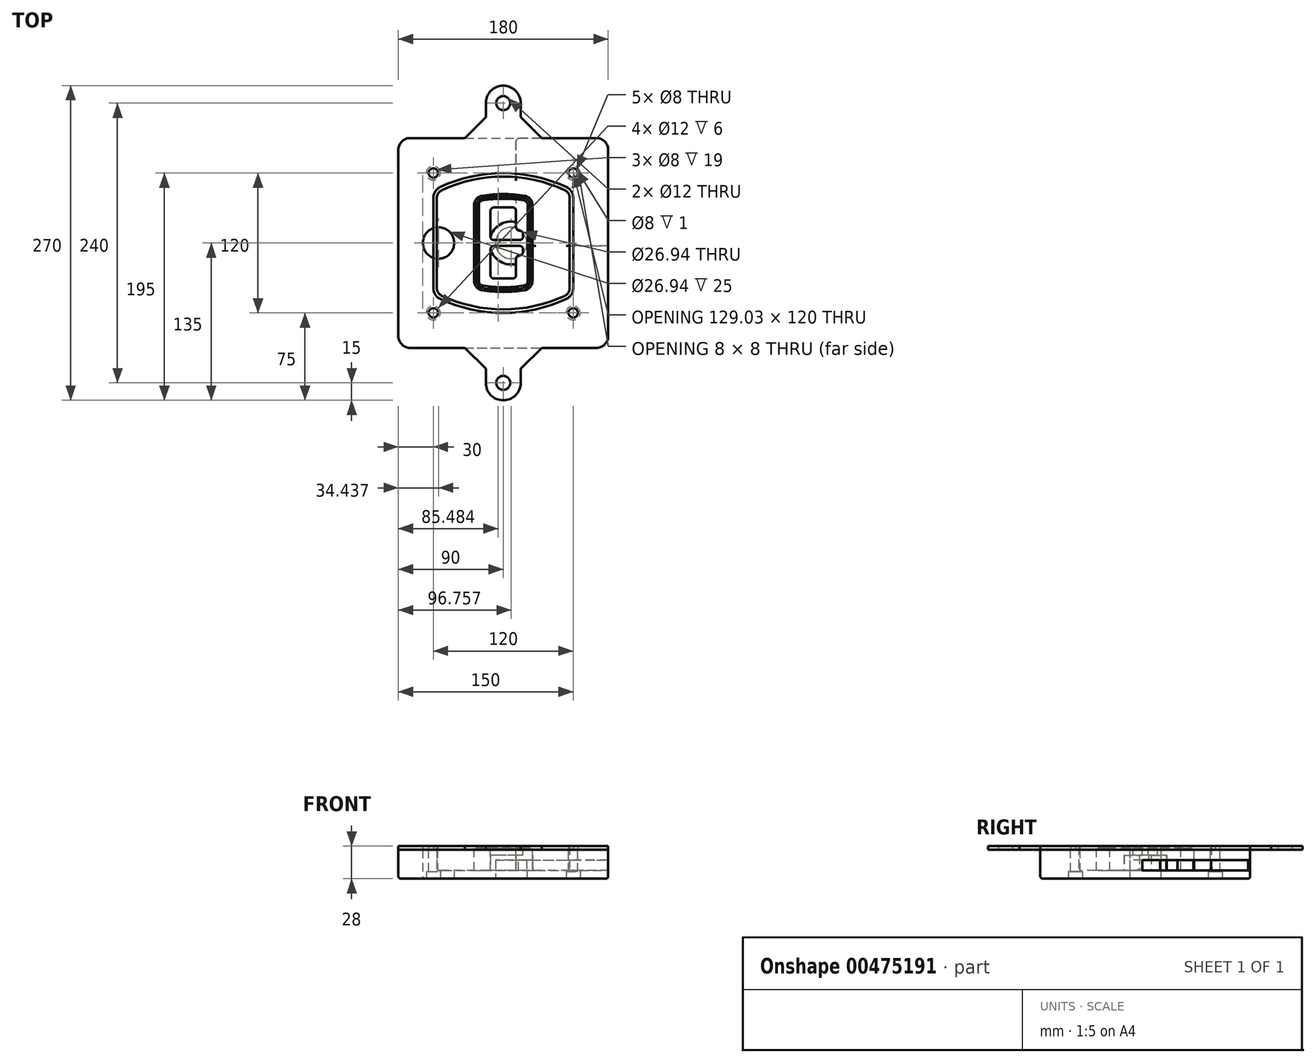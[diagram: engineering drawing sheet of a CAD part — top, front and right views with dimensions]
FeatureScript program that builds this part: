
annotation { "Feature Type Name" : "Feature", "Feature Type Description" : "" }
export const myFeature = defineFeature(function(context is Context, id is Id, definition is map)
    precondition{}
    {
        {
            var Q0;
            Q0=qCreatedBy(makeId("Top.planeOp"),FACE);
            var sketch = newSketch(context, id + "F0", { "sketchPlane" : qUnion([Q0])});
            skPoint(sketch, "E0.rect.middle", {"position": v(0, 0) * mm});
            skLineSegment(sketch, "E1.bottom", {"start": v(-80, -90) * mm, "end": v(80, -90) * mm});
            skLineSegment(sketch, "E1.top", {"start": v(-80, 90) * mm, "end": v(80, 90) * mm});
            skLineSegment(sketch, "E1.left", {"start": v(-90, -80) * mm, "end": v(-90, 80) * mm});
            skLineSegment(sketch, "E1.right", {"start": v(90, -80) * mm, "end": v(90, 80) * mm});
            skLineSegment(sketch, "E2", {"start": v(-90, 90) * mm, "end": v(90, -90) * mm, "construction": true});
            skLineSegment(sketch, "E3", {"start": v(90, 90) * mm, "end": v(-90, -90) * mm, "construction": true});
            skCircle(sketch, "E4", {"center": v(-60, 60) * mm, "radius": 4 * mm});
            skCircle(sketch, "E5", {"center": v(60, 60) * mm, "radius": 4 * mm});
            skCircle(sketch, "E6", {"center": v(60, -60) * mm, "radius": 4 * mm});
            skCircle(sketch, "E7", {"center": v(-60, -60) * mm, "radius": 4 * mm});
            skLineSegment(sketch, "E8", {"start": v(-60, 60) * mm, "end": v(60, 60) * mm, "construction": true});
            skLineSegment(sketch, "E9", {"start": v(60, 60) * mm, "end": v(60, -60) * mm, "construction": true});
            skLineSegment(sketch, "E10", {"start": v(60, -60) * mm, "end": v(-60, -60) * mm, "construction": true});
            skLineSegment(sketch, "E11", {"start": v(-60, -60) * mm, "end": v(-60, 60) * mm, "construction": true});
            skLineSegment(sketch, "E12", {"start": v(-60, 38.83) * mm, "end": v(-60, -38.83) * mm});
            skLineSegment(sketch, "E13", {"start": v(60, 38.83) * mm, "end": v(60, -38.83) * mm});
            skArc(sketch, "E14", {"start": v(54.26, 47.88) * mm, "mid": v(0, 60) * mm, "end": v(-54.26, 47.88) * mm});
            skArc(sketch, "E15", {"start": v(-54.26, -47.88) * mm, "mid": v(0, -60) * mm, "end": v(54.26, -47.88) * mm});
            skLineSegment(sketch, "E16", {"start": v(-60, 0) * mm, "end": v(60, 0) * mm, "construction": true});
            skPoint(sketch, "E17.visualSharp", {"position": v(-60, -45) * mm});
            skArc(sketch, "E17.filletArc", {"start": v(-60, -38.83) * mm, "mid": v(-58.44, -44.2) * mm, "end": v(-54.26, -47.88) * mm});
            skPoint(sketch, "E18.visualSharp", {"position": v(-60, 45) * mm});
            skArc(sketch, "E18.filletArc", {"start": v(-54.26, 47.88) * mm, "mid": v(-58.44, 44.2) * mm, "end": v(-60, 38.83) * mm});
            skPoint(sketch, "E19.visualSharp", {"position": v(60, 45) * mm});
            skArc(sketch, "E19.filletArc", {"start": v(60, 38.83) * mm, "mid": v(58.44, 44.2) * mm, "end": v(54.26, 47.88) * mm});
            skPoint(sketch, "E20.visualSharp", {"position": v(60, -45) * mm});
            skArc(sketch, "E20.filletArc", {"start": v(54.26, -47.88) * mm, "mid": v(58.44, -44.2) * mm, "end": v(60, -38.83) * mm});
            skPoint(sketch, "E21.visualSharp", {"position": v(-90, 90) * mm});
            skArc(sketch, "E21.filletArc", {"start": v(-80, 90) * mm, "mid": v(-87.07, 87.07) * mm, "end": v(-90, 80) * mm});
            skPoint(sketch, "E22.visualSharp", {"position": v(90, 90) * mm});
            skArc(sketch, "E22.filletArc", {"start": v(90, 80) * mm, "mid": v(87.07, 87.07) * mm, "end": v(80, 90) * mm});
            skPoint(sketch, "E23.visualSharp", {"position": v(90, -90) * mm});
            skArc(sketch, "E23.filletArc", {"start": v(80, -90) * mm, "mid": v(87.07, -87.07) * mm, "end": v(90, -80) * mm});
            skPoint(sketch, "E24.visualSharp", {"position": v(-90, -90) * mm});
            skArc(sketch, "E24.filletArc", {"start": v(-90, -80) * mm, "mid": v(-87.07, -87.07) * mm, "end": v(-80, -90) * mm});
            skArc(sketch, "E25.0", {"start": v(57, 38.83) * mm, "mid": v(55.9, 42.58) * mm, "end": v(52.98, 45.17) * mm});
            skLineSegment(sketch, "E25.1", {"start": v(57, 38.83) * mm, "end": v(57, -38.83) * mm});
            skArc(sketch, "E25.2", {"start": v(52.98, -45.17) * mm, "mid": v(55.9, -42.58) * mm, "end": v(57, -38.83) * mm});
            skArc(sketch, "E25.3", {"start": v(-52.98, -45.17) * mm, "mid": v(0, -57) * mm, "end": v(52.98, -45.17) * mm});
            skArc(sketch, "E25.4", {"start": v(-57, -38.83) * mm, "mid": v(-55.9, -42.58) * mm, "end": v(-52.98, -45.17) * mm});
            skArc(sketch, "E25.5", {"start": v(52.98, 45.17) * mm, "mid": v(0, 57) * mm, "end": v(-52.98, 45.17) * mm});
            skLineSegment(sketch, "E25.6", {"start": v(-57, 38.83) * mm, "end": v(-57, -38.83) * mm});
            skArc(sketch, "E25.7", {"start": v(-52.98, 45.17) * mm, "mid": v(-55.9, 42.58) * mm, "end": v(-57, 38.83) * mm});
            skArc(sketch, "E26.0", {"start": v(-55.96, 51.5) * mm, "mid": v(-61.82, 46.33) * mm, "end": v(-64, 38.83) * mm});
            skArc(sketch, "E26.1", {"start": v(55.96, 51.5) * mm, "mid": v(0, 64) * mm, "end": v(-55.96, 51.5) * mm});
            skArc(sketch, "E26.2", {"start": v(64, 38.83) * mm, "mid": v(61.82, 46.33) * mm, "end": v(55.96, 51.5) * mm});
            skLineSegment(sketch, "E26.3", {"start": v(64, 38.83) * mm, "end": v(64, -38.83) * mm});
            skArc(sketch, "E26.4", {"start": v(55.96, -51.5) * mm, "mid": v(61.82, -46.33) * mm, "end": v(64, -38.83) * mm});
            skLineSegment(sketch, "E26.5", {"start": v(-64, 38.83) * mm, "end": v(-64, -38.83) * mm});
            skArc(sketch, "E26.6", {"start": v(-55.96, -51.5) * mm, "mid": v(0, -64) * mm, "end": v(55.96, -51.5) * mm});
            skArc(sketch, "E26.7", {"start": v(-64, -38.83) * mm, "mid": v(-61.82, -46.33) * mm, "end": v(-55.96, -51.5) * mm});
            skSolve(sketch);
        }
        {
            var Q0;
            Q0=makeQuery(id+"F0.imprint","IMPRINT",FACE,{"disambiguationData":[TD([[makeQuery(id+"F0.imprint","IMPRINT",EDGE,{"derivedFrom":sQuery(id+"F0.wireOp",EDGE,"E1.bottom")}),1.0]])]});
            var Q1;
            Q1=makeQuery(id+"F0.imprint","IMPRINT",FACE,{"disambiguationData":[TD([[makeQuery(id+"F0.imprint","IMPRINT",EDGE,{"derivedFrom":sQuery(id+"F0.wireOp",EDGE,"E12")}),1.0]])]});
            var Q2;
            Q2=makeQuery(id+"F0.imprint","IMPRINT",FACE,{"disambiguationData":[TD([[makeQuery(id+"F0.imprint","IMPRINT",EDGE,{"derivedFrom":sQuery(id+"F0.wireOp",EDGE,"E25.0")}),1.0]])]});
            var Q3;
            Q3=makeQuery(id+"F0.imprint","IMPRINT",FACE,{"disambiguationData":[TD([[makeQuery(id+"F0.imprint","IMPRINT",EDGE,{"derivedFrom":sQuery(id+"F0.wireOp",EDGE,"E12")}),-1.0]])]});
            extrude(context, id + "F1", {"entities" : qUnion([Q0, Q1, Q2, Q3]), "oppositeDirection" : true, "depth" : 25 * mm});
        }
        {
            var Q0;
            Q0=makeQuery(id+"F0.imprint","IMPRINT",FACE,{"disambiguationData":[TD([[makeQuery(id+"F0.imprint","IMPRINT",EDGE,{"derivedFrom":sQuery(id+"F0.wireOp",EDGE,"E12")}),1.0]])]});
            extrude(context, id + "F2", {"entities" : qUnion([Q0]), "operationType" : NewBodyOperationType.ADD, "depth" : 3 * mm});
        }
        {
            var Q0;
            Q0=makeQuery(id+"F0.imprint","IMPRINT",FACE,{"disambiguationData":[TD([[makeQuery(id+"F0.imprint","IMPRINT",EDGE,{"derivedFrom":sQuery(id+"F0.wireOp",EDGE,"E25.0")}),1.0]])]});
            extrude(context, id + "F3", {"entities" : qUnion([Q0]), "operationType" : NewBodyOperationType.REMOVE, "oppositeDirection" : true, "depth" : 18 * mm});
        }
        {
            var Q0;
            Q0=makeQuery(id+"F2.opExtrude","CAP_FACE",FACE,{"disambiguationData":[OSD([sQuery(id+"F0.wireOp",EDGE,"E12"),sQuery(id+"F0.wireOp",EDGE,"E13"),sQuery(id+"F0.wireOp",EDGE,"E14"),sQuery(id+"F0.wireOp",EDGE,"E15"),sQuery(id+"F0.wireOp",EDGE,"E17.filletArc"),sQuery(id+"F0.wireOp",EDGE,"E18.filletArc"),sQuery(id+"F0.wireOp",EDGE,"E19.filletArc"),sQuery(id+"F0.wireOp",EDGE,"E20.filletArc"),sQuery(id+"F0.wireOp",EDGE,"E25.0"),sQuery(id+"F0.wireOp",EDGE,"E25.1"),sQuery(id+"F0.wireOp",EDGE,"E25.2"),sQuery(id+"F0.wireOp",EDGE,"E25.3"),sQuery(id+"F0.wireOp",EDGE,"E25.4"),sQuery(id+"F0.wireOp",EDGE,"E25.5"),sQuery(id+"F0.wireOp",EDGE,"E25.6"),sQuery(id+"F0.wireOp",EDGE,"E25.7")])],"isStart":false});
            var sketch = newSketch(context, id + "F4", { "sketchPlane" : qUnion([Q0])});
            skArc(sketch, "E27.0", {"start": v(-18.34, -40.45) * mm, "mid": v(0, -42) * mm, "end": v(18.34, -40.45) * mm});
            skArc(sketch, "E28.0", {"start": v(18.34, 40.45) * mm, "mid": v(0, 42) * mm, "end": v(-18.34, 40.45) * mm});
            skLineSegment(sketch, "E29", {"start": v(-25, 32.57) * mm, "end": v(-25, -32.57) * mm});
            skLineSegment(sketch, "E30", {"start": v(25, 32.57) * mm, "end": v(25, -32.57) * mm});
            skLineSegment(sketch, "E31", {"start": v(-25, 39.1) * mm, "end": v(25, 39.1) * mm, "construction": true});
            skLineSegment(sketch, "E32", {"start": v(-25, -39.1) * mm, "end": v(25, -39.1) * mm, "construction": true});
            skPoint(sketch, "E33.visualSharp", {"position": v(-25, 39.1) * mm});
            skArc(sketch, "E33.filletArc", {"start": v(-18.34, 40.45) * mm, "mid": v(-23.11, 37.73) * mm, "end": v(-25, 32.57) * mm});
            skPoint(sketch, "E34.visualSharp", {"position": v(25, 39.1) * mm});
            skArc(sketch, "E34.filletArc", {"start": v(25, 32.57) * mm, "mid": v(23.11, 37.73) * mm, "end": v(18.34, 40.45) * mm});
            skPoint(sketch, "E35.visualSharp", {"position": v(25, -39.1) * mm});
            skArc(sketch, "E35.filletArc", {"start": v(18.34, -40.45) * mm, "mid": v(23.11, -37.73) * mm, "end": v(25, -32.57) * mm});
            skPoint(sketch, "E36.visualSharp", {"position": v(-25, -39.1) * mm});
            skArc(sketch, "E36.filletArc", {"start": v(-25, -32.57) * mm, "mid": v(-23.11, -37.73) * mm, "end": v(-18.34, -40.45) * mm});
            skArc(sketch, "E37.0", {"start": v(52.98, 45.17) * mm, "mid": v(0, 57) * mm, "end": v(-52.98, 45.17) * mm});
            skArc(sketch, "E37.1", {"start": v(-52.98, 45.17) * mm, "mid": v(-55.9, 42.58) * mm, "end": v(-57, 38.83) * mm});
            skLineSegment(sketch, "E37.2", {"start": v(-57, 38.83) * mm, "end": v(-57, -38.83) * mm});
            skArc(sketch, "E37.3", {"start": v(-57, -38.83) * mm, "mid": v(-55.9, -42.58) * mm, "end": v(-52.98, -45.17) * mm});
            skArc(sketch, "E37.4", {"start": v(-52.98, -45.17) * mm, "mid": v(0, -57) * mm, "end": v(52.98, -45.17) * mm});
            skArc(sketch, "E37.5", {"start": v(52.98, -45.17) * mm, "mid": v(55.9, -42.58) * mm, "end": v(57, -38.83) * mm});
            skLineSegment(sketch, "E37.6", {"start": v(57, 38.83) * mm, "end": v(57, -38.83) * mm});
            skArc(sketch, "E37.7", {"start": v(57, 38.83) * mm, "mid": v(55.9, 42.58) * mm, "end": v(52.98, 45.17) * mm});
            skLineSegment(sketch, "E38.0", {"start": v(23, 32.57) * mm, "end": v(23, -32.57) * mm});
            skArc(sketch, "E38.1", {"start": v(18, -38.48) * mm, "mid": v(21.58, -36.44) * mm, "end": v(23, -32.57) * mm});
            skArc(sketch, "E38.2", {"start": v(-18, -38.48) * mm, "mid": v(0, -40) * mm, "end": v(18, -38.48) * mm});
            skArc(sketch, "E38.3", {"start": v(-23, -32.57) * mm, "mid": v(-21.58, -36.44) * mm, "end": v(-18, -38.48) * mm});
            skLineSegment(sketch, "E38.4", {"start": v(-23, 32.57) * mm, "end": v(-23, -32.57) * mm});
            skArc(sketch, "E38.5", {"start": v(23, 32.57) * mm, "mid": v(21.58, 36.44) * mm, "end": v(18, 38.48) * mm});
            skArc(sketch, "E38.6", {"start": v(-18, 38.48) * mm, "mid": v(-21.58, 36.44) * mm, "end": v(-23, 32.57) * mm});
            skArc(sketch, "E38.7", {"start": v(18, 38.48) * mm, "mid": v(0, 40) * mm, "end": v(-18, 38.48) * mm});
            skArc(sketch, "E39.0", {"start": v(21, 32.57) * mm, "mid": v(20.06, 35.15) * mm, "end": v(17.67, 36.5) * mm});
            skLineSegment(sketch, "E39.1", {"start": v(21, 32.57) * mm, "end": v(21, -32.57) * mm});
            skArc(sketch, "E39.2", {"start": v(17.67, -36.5) * mm, "mid": v(20.06, -35.15) * mm, "end": v(21, -32.57) * mm});
            skArc(sketch, "E39.3", {"start": v(-17.67, -36.5) * mm, "mid": v(0, -38) * mm, "end": v(17.67, -36.5) * mm});
            skArc(sketch, "E39.4", {"start": v(-21, -32.57) * mm, "mid": v(-20.06, -35.15) * mm, "end": v(-17.67, -36.5) * mm});
            skArc(sketch, "E39.5", {"start": v(17.67, 36.5) * mm, "mid": v(0, 38) * mm, "end": v(-17.67, 36.5) * mm});
            skLineSegment(sketch, "E39.6", {"start": v(-21, 32.57) * mm, "end": v(-21, -32.57) * mm});
            skArc(sketch, "E39.7", {"start": v(-17.67, 36.5) * mm, "mid": v(-20.06, 35.15) * mm, "end": v(-21, 32.57) * mm});
            skLineSegment(sketch, "E40", {"start": v(-25, 0) * mm, "end": v(25, 0) * mm, "construction": true});
            skLineSegment(sketch, "E41", {"start": v(-11, 5.5) * mm, "end": v(-11, 27.5) * mm});
            skLineSegment(sketch, "E42", {"start": v(-8, 30.5) * mm, "end": v(8, 30.5) * mm});
            skLineSegment(sketch, "E43", {"start": v(11, 27.5) * mm, "end": v(11, 13.5) * mm});
            skLineSegment(sketch, "E44", {"start": v(14, 10.5) * mm, "end": v(14, 10.5) * mm});
            skLineSegment(sketch, "E45", {"start": v(17, 7.5) * mm, "end": v(17, 5.5) * mm});
            skLineSegment(sketch, "E46", {"start": v(14, 2.5) * mm, "end": v(-8, 2.5) * mm});
            skPoint(sketch, "E47.visualSharp", {"position": v(-11, 30.5) * mm});
            skArc(sketch, "E47.filletArc", {"start": v(-8, 30.5) * mm, "mid": v(-10.12, 29.62) * mm, "end": v(-11, 27.5) * mm});
            skPoint(sketch, "E48.visualSharp", {"position": v(11, 30.5) * mm});
            skArc(sketch, "E48.filletArc", {"start": v(11, 27.5) * mm, "mid": v(10.12, 29.62) * mm, "end": v(8, 30.5) * mm});
            skPoint(sketch, "E49.visualSharp", {"position": v(11, 10.5) * mm});
            skArc(sketch, "E49.filletArc", {"start": v(11, 13.5) * mm, "mid": v(11.88, 11.38) * mm, "end": v(14, 10.5) * mm});
            skPoint(sketch, "E50.visualSharp", {"position": v(17, 10.5) * mm});
            skArc(sketch, "E50.filletArc", {"start": v(17, 7.5) * mm, "mid": v(16.12, 9.62) * mm, "end": v(14, 10.5) * mm});
            skPoint(sketch, "E51.visualSharp", {"position": v(17, 2.5) * mm});
            skArc(sketch, "E51.filletArc", {"start": v(14, 2.5) * mm, "mid": v(16.12, 3.38) * mm, "end": v(17, 5.5) * mm});
            skPoint(sketch, "E52.visualSharp", {"position": v(-11, 2.5) * mm});
            skArc(sketch, "E52.filletArc", {"start": v(-11, 5.5) * mm, "mid": v(-10.12, 3.38) * mm, "end": v(-8, 2.5) * mm});
            skLineSegment(sketch, "E53.0.MirrorCS", {"start": v(14, -2.5) * mm, "end": v(-8, -2.5) * mm});
            skArc(sketch, "E54.0.MirrorCS", {"start": v(-11, -5.5) * mm, "mid": v(-10.12, -3.38) * mm, "end": v(-8, -2.5) * mm});
            skLineSegment(sketch, "E55.0.MirrorCS", {"start": v(-11, -5.5) * mm, "end": v(-11, -27.5) * mm});
            skArc(sketch, "E56.0.MirrorCS", {"start": v(-8, -30.5) * mm, "mid": v(-10.12, -29.62) * mm, "end": v(-11, -27.5) * mm});
            skLineSegment(sketch, "E57.0.MirrorCS", {"start": v(-8, -30.5) * mm, "end": v(8, -30.5) * mm});
            skArc(sketch, "E58.0.MirrorCS", {"start": v(11, -27.5) * mm, "mid": v(10.12, -29.62) * mm, "end": v(8, -30.5) * mm});
            skLineSegment(sketch, "E59.0.MirrorCS", {"start": v(11, -27.5) * mm, "end": v(11, -13.5) * mm});
            skArc(sketch, "E60.0.MirrorCS", {"start": v(11, -13.5) * mm, "mid": v(11.88, -11.38) * mm, "end": v(14, -10.5) * mm});
            skArc(sketch, "E61.0.MirrorCS", {"start": v(17, -7.5) * mm, "mid": v(16.12, -9.62) * mm, "end": v(14, -10.5) * mm});
            skLineSegment(sketch, "E62.0.MirrorCS", {"start": v(17, -7.5) * mm, "end": v(17, -5.5) * mm});
            skArc(sketch, "E63.0.MirrorCS", {"start": v(14, -2.5) * mm, "mid": v(16.12, -3.38) * mm, "end": v(17, -5.5) * mm});
            skSolve(sketch);
        }
        {
            var Q0;
            Q0=makeQuery(id+"F4.imprint","IMPRINT",FACE,{"disambiguationData":[TD([[makeQuery(id+"F4.imprint","IMPRINT",EDGE,{"derivedFrom":sQuery(id+"F4.wireOp",EDGE,"E27.0")}),1.0]])]});
            var Q1;
            Q1=makeQuery(id+"F4.imprint","IMPRINT",FACE,{"disambiguationData":[TD([[makeQuery(id+"F4.imprint","IMPRINT",EDGE,{"derivedFrom":sQuery(id+"F4.wireOp",EDGE,"E38.0")}),-1.0]])]});
            var Q2;
            Q2=makeQuery(id+"F4.imprint","IMPRINT",FACE,{"disambiguationData":[TD([[makeQuery(id+"F4.imprint","IMPRINT",EDGE,{"derivedFrom":sQuery(id+"F4.wireOp",EDGE,"E39.0")}),1.0]])]});
            extrude(context, id + "F5", {"entities" : qUnion([Q0, Q1, Q2]), "operationType" : NewBodyOperationType.ADD, "endBound" : BoundingType.UP_TO_NEXT, "oppositeDirection" : true, "depth" : 25 * mm});
        }
        {
            var Q0;
            Q0=makeQuery(id+"F4.imprint","IMPRINT",FACE,{"disambiguationData":[TD([[makeQuery(id+"F4.imprint","IMPRINT",EDGE,{"derivedFrom":sQuery(id+"F4.wireOp",EDGE,"E38.0")}),-1.0]])]});
            extrude(context, id + "F6", {"entities" : qUnion([Q0]), "operationType" : NewBodyOperationType.REMOVE, "oppositeDirection" : true, "depth" : 2 * mm});
        }
        {
            var Q0;
            Q0=makeQuery(id+"F1.opExtrude","CAP_FACE",FACE,{"disambiguationData":[OSD([sQuery(id+"F0.wireOp",EDGE,"E1.bottom"),sQuery(id+"F0.wireOp",EDGE,"E1.top"),sQuery(id+"F0.wireOp",EDGE,"E1.left"),sQuery(id+"F0.wireOp",EDGE,"E1.right"),sQuery(id+"F0.wireOp",EDGE,"E4"),sQuery(id+"F0.wireOp",EDGE,"E5"),sQuery(id+"F0.wireOp",EDGE,"E6"),sQuery(id+"F0.wireOp",EDGE,"E7"),sQuery(id+"F0.wireOp",EDGE,"E21.filletArc"),sQuery(id+"F0.wireOp",EDGE,"E22.filletArc"),sQuery(id+"F0.wireOp",EDGE,"E23.filletArc"),sQuery(id+"F0.wireOp",EDGE,"E24.filletArc")])],"isStart":false});
            var sketch = newSketch(context, id + "F7", { "sketchPlane" : qUnion([Q0])});
            skCircle(sketch, "E64", {"center": v(6.76, 0) * mm, "radius": 13.47 * mm});
            skCircle(sketch, "E65", {"center": v(-55.56, 0) * mm, "radius": 13.47 * mm});
            skLineSegment(sketch, "E66", {"start": v(90, 0) * mm, "end": v(-90, 0) * mm});
            skCircle(sketch, "E67", {"center": v(6.76, 0) * mm, "radius": 18.47 * mm});
            skCircle(sketch, "E68", {"center": v(60, -60) * mm, "radius": 6 * mm});
            skCircle(sketch, "E69", {"center": v(-60, -60) * mm, "radius": 6 * mm});
            skCircle(sketch, "E70", {"center": v(-60, 60) * mm, "radius": 6 * mm});
            skCircle(sketch, "E71", {"center": v(60, 60) * mm, "radius": 6 * mm});
            skSolve(sketch);
        }
        {
            var Q0;
            {var subQ1=sQuery(id+"F7.wireOp",EDGE,"E66");var subQ4=sQuery(id+"F7.wireOp",EDGE,"E64");var subQ6=makeQuery(id+"F7.imprint","INTERSECT",VERTEX,{"disambiguationData":[OD(0.0)],"derivedFrom":[subQ4,subQ1]});Q0=makeQuery(id+"F7.imprint","IMPRINT",FACE,{"disambiguationData":[TD([[makeQuery(id+"F7.imprint","IMPRINT",EDGE,{"disambiguationData":[TD([[subQ6,-1.0]])],"derivedFrom":subQ4}),-1.0]])]});}
            var Q1;
            {var subQ0=sQuery(id+"F7.wireOp",EDGE,"E66");var subQ1=sQuery(id+"F7.wireOp",EDGE,"E64");var subQ3=makeQuery(id+"F7.imprint","INTERSECT",VERTEX,{"disambiguationData":[OD(0.0)],"derivedFrom":[subQ1,subQ0]});Q1=makeQuery(id+"F7.imprint","IMPRINT",FACE,{"disambiguationData":[TD([[makeQuery(id+"F7.imprint","IMPRINT",EDGE,{"disambiguationData":[TD([[subQ3,-1.0]])],"derivedFrom":subQ1}),1.0]])]});}
            var Q2;
            {var subQ0=sQuery(id+"F7.wireOp",EDGE,"E66");var subQ1=sQuery(id+"F7.wireOp",EDGE,"E64");var subQ3=makeQuery(id+"F7.imprint","INTERSECT",VERTEX,{"disambiguationData":[OD(0.0)],"derivedFrom":[subQ1,subQ0]});Q2=makeQuery(id+"F7.imprint","IMPRINT",FACE,{"disambiguationData":[TD([[makeQuery(id+"F7.imprint","IMPRINT",EDGE,{"disambiguationData":[TD([[subQ3,1.0]])],"derivedFrom":subQ1}),1.0]])]});}
            var Q3;
            {var subQ1=sQuery(id+"F7.wireOp",EDGE,"E66");var subQ4=sQuery(id+"F7.wireOp",EDGE,"E64");var subQ6=makeQuery(id+"F7.imprint","INTERSECT",VERTEX,{"disambiguationData":[OD(0.0)],"derivedFrom":[subQ4,subQ1]});Q3=makeQuery(id+"F7.imprint","IMPRINT",FACE,{"disambiguationData":[TD([[makeQuery(id+"F7.imprint","IMPRINT",EDGE,{"disambiguationData":[TD([[subQ6,1.0]])],"derivedFrom":subQ4}),-1.0]])]});}
            extrude(context, id + "F8", {"entities" : qUnion([Q0, Q1, Q2, Q3]), "operationType" : NewBodyOperationType.ADD, "oppositeDirection" : true, "depth" : 20 * mm});
        }
        {
            var Q0;
            {var subQ0=sQuery(id+"F7.wireOp",EDGE,"E66");var subQ1=sQuery(id+"F7.wireOp",EDGE,"E64");var subQ3=makeQuery(id+"F7.imprint","INTERSECT",VERTEX,{"disambiguationData":[OD(0.0)],"derivedFrom":[subQ1,subQ0]});Q0=makeQuery(id+"F7.imprint","IMPRINT",FACE,{"disambiguationData":[TD([[makeQuery(id+"F7.imprint","IMPRINT",EDGE,{"disambiguationData":[TD([[subQ3,-1.0]])],"derivedFrom":subQ1}),1.0]])]});}
            var Q1;
            {var subQ0=sQuery(id+"F7.wireOp",EDGE,"E66");var subQ1=sQuery(id+"F7.wireOp",EDGE,"E64");var subQ3=makeQuery(id+"F7.imprint","INTERSECT",VERTEX,{"disambiguationData":[OD(0.0)],"derivedFrom":[subQ1,subQ0]});Q1=makeQuery(id+"F7.imprint","IMPRINT",FACE,{"disambiguationData":[TD([[makeQuery(id+"F7.imprint","IMPRINT",EDGE,{"disambiguationData":[TD([[subQ3,1.0]])],"derivedFrom":subQ1}),1.0]])]});}
            extrude(context, id + "F9", {"entities" : qUnion([Q0, Q1]), "operationType" : NewBodyOperationType.REMOVE, "oppositeDirection" : true, "depth" : 16 * mm});
        }
        {
            var Q0;
            {var subQ0=sQuery(id+"F7.wireOp",EDGE,"E66");var subQ1=sQuery(id+"F7.wireOp",EDGE,"E65");var subQ3=makeQuery(id+"F7.imprint","INTERSECT",VERTEX,{"disambiguationData":[OD(0.0)],"derivedFrom":[subQ1,subQ0]});Q0=makeQuery(id+"F7.imprint","IMPRINT",FACE,{"disambiguationData":[TD([[makeQuery(id+"F7.imprint","IMPRINT",EDGE,{"disambiguationData":[TD([[subQ3,-1.0]])],"derivedFrom":subQ1}),1.0]])]});}
            var Q1;
            {var subQ0=sQuery(id+"F7.wireOp",EDGE,"E66");var subQ1=sQuery(id+"F7.wireOp",EDGE,"E65");var subQ3=makeQuery(id+"F7.imprint","INTERSECT",VERTEX,{"disambiguationData":[OD(0.0)],"derivedFrom":[subQ1,subQ0]});Q1=makeQuery(id+"F7.imprint","IMPRINT",FACE,{"disambiguationData":[TD([[makeQuery(id+"F7.imprint","IMPRINT",EDGE,{"disambiguationData":[TD([[subQ3,1.0]])],"derivedFrom":subQ1}),1.0]])]});}
            extrude(context, id + "F10", {"entities" : qUnion([Q0, Q1]), "operationType" : NewBodyOperationType.REMOVE, "oppositeDirection" : true, "depth" : 25 * mm});
        }
        {
            var Q0;
            Q0=makeQuery(id+"F7.imprint","IMPRINT",FACE,{"disambiguationData":[TD([[makeQuery(id+"F7.imprint","IMPRINT",EDGE,{"derivedFrom":sQuery(id+"F7.wireOp",EDGE,"E68")}),1.0]])]});
            var Q1;
            Q1=makeQuery(id+"F7.imprint","IMPRINT",FACE,{"disambiguationData":[TD([[makeQuery(id+"F7.imprint","IMPRINT",EDGE,{"derivedFrom":makeQuery(id+"F1.opExtrude","CAP_EDGE",EDGE,{"disambiguationData":[OSD([sQuery(id+"F0.wireOp",EDGE,"E5")])],"isStart":false})}),-1.0]])]});
            var Q2;
            Q2=makeQuery(id+"F7.imprint","IMPRINT",FACE,{"disambiguationData":[TD([[makeQuery(id+"F7.imprint","IMPRINT",EDGE,{"derivedFrom":sQuery(id+"F7.wireOp",EDGE,"E69")}),1.0]])]});
            var Q3;
            Q3=makeQuery(id+"F7.imprint","IMPRINT",FACE,{"disambiguationData":[TD([[makeQuery(id+"F7.imprint","IMPRINT",EDGE,{"derivedFrom":makeQuery(id+"F1.opExtrude","CAP_EDGE",EDGE,{"disambiguationData":[OSD([sQuery(id+"F0.wireOp",EDGE,"E4")])],"isStart":false})}),-1.0]])]});
            var Q4;
            Q4=makeQuery(id+"F7.imprint","IMPRINT",FACE,{"disambiguationData":[TD([[makeQuery(id+"F7.imprint","IMPRINT",EDGE,{"derivedFrom":sQuery(id+"F7.wireOp",EDGE,"E70")}),1.0]])]});
            var Q5;
            Q5=makeQuery(id+"F7.imprint","IMPRINT",FACE,{"disambiguationData":[TD([[makeQuery(id+"F7.imprint","IMPRINT",EDGE,{"derivedFrom":makeQuery(id+"F1.opExtrude","CAP_EDGE",EDGE,{"disambiguationData":[OSD([sQuery(id+"F0.wireOp",EDGE,"E7")])],"isStart":false})}),-1.0]])]});
            var Q6;
            Q6=makeQuery(id+"F7.imprint","IMPRINT",FACE,{"disambiguationData":[TD([[makeQuery(id+"F7.imprint","IMPRINT",EDGE,{"derivedFrom":sQuery(id+"F7.wireOp",EDGE,"E71")}),1.0]])]});
            var Q7;
            Q7=makeQuery(id+"F7.imprint","IMPRINT",FACE,{"disambiguationData":[TD([[makeQuery(id+"F7.imprint","IMPRINT",EDGE,{"derivedFrom":makeQuery(id+"F1.opExtrude","CAP_EDGE",EDGE,{"disambiguationData":[OSD([sQuery(id+"F0.wireOp",EDGE,"E6")])],"isStart":false})}),-1.0]])]});
            extrude(context, id + "F11", {"entities" : qUnion([Q0, Q1, Q2, Q3, Q4, Q5, Q6, Q7]), "operationType" : NewBodyOperationType.REMOVE, "oppositeDirection" : true, "depth" : 6 * mm});
        }
        {
            var Q0;
            Q0=makeQuery(id+"F9.boolean.opBoolean","COPY",FACE,{"derivedFrom":makeQuery(id+"F9.opExtrude","CAP_FACE",FACE,{"disambiguationData":[OSD([sQuery(id+"F7.wireOp",EDGE,"E64")])],"isStart":false})});
            var sketch = newSketch(context, id + "F12", { "sketchPlane" : qUnion([Q0])});
            skArc(sketch, "E72.0", {"start": v(11, -88.19) * mm, "mid": v(97.1, -83.6) * mm, "end": v(92.5, 2.5) * mm});
            skLineSegment(sketch, "E72.1", {"start": v(11, -17.97) * mm, "end": v(11, -17.97) * mm});
            skLineSegment(sketch, "E73", {"start": v(92.5, -105.13) * mm, "end": v(102.3, -105.13) * mm});
            skLineSegment(sketch, "E74.0", {"start": v(92.5, 2.5) * mm, "end": v(14, 2.5) * mm});
            skArc(sketch, "E74.1", {"start": v(14, 2.5) * mm, "mid": v(16.12, 3.38) * mm, "end": v(17, 5.5) * mm});
            skLineSegment(sketch, "E74.2", {"start": v(17, 7.5) * mm, "end": v(17, 5.5) * mm});
            skArc(sketch, "E74.3", {"start": v(17, 7.5) * mm, "mid": v(16.12, 9.62) * mm, "end": v(14, 10.5) * mm});
            skArc(sketch, "E74.4", {"start": v(11, 13.5) * mm, "mid": v(11.88, 11.38) * mm, "end": v(14, 10.5) * mm});
            skLineSegment(sketch, "E74.5", {"start": v(11, 13.5) * mm, "end": v(11, -88.19) * mm});
            skLineSegment(sketch, "E74.7", {"start": v(92.5, -2.5) * mm, "end": v(14, -2.5) * mm});
            skArc(sketch, "E74.8", {"start": v(14, -2.5) * mm, "mid": v(16.12, -3.38) * mm, "end": v(17, -5.5) * mm});
            skLineSegment(sketch, "E74.9", {"start": v(17, -7.5) * mm, "end": v(17, -5.5) * mm});
            skArc(sketch, "E74.10", {"start": v(17, -7.5) * mm, "mid": v(16.12, -9.62) * mm, "end": v(14, -10.5) * mm});
            skArc(sketch, "E74.11", {"start": v(11, -13.5) * mm, "mid": v(11.88, -11.38) * mm, "end": v(14, -10.5) * mm});
            skLineSegment(sketch, "E74.12", {"start": v(11, -17.97) * mm, "end": v(11, -13.5) * mm});
            skPoint(sketch, "E75.orphan", {"position": v(11, -27.5) * mm});
            skPoint(sketch, "E76.orphan", {"position": v(-8, -2.5) * mm});
            skPoint(sketch, "E77.orphan", {"position": v(-8, 2.5) * mm});
            skPoint(sketch, "E78.orphan", {"position": v(11, 27.5) * mm});
            skSolve(sketch);
        }
        {
            var Q0;
            {var subQ7=sQuery(id+"F12.wireOp",EDGE,"E72.0");var subQ14=sQuery(id+"F12.wireOp",EDGE,"E72.1");var subQ16=sQuery(id+"F12.wireOp",EDGE,"E74.1");var subQ18=sQuery(id+"F12.wireOp",EDGE,"E74.8");Q0=qUnion([makeQuery(id+"F12.imprint","IMPRINT",FACE,{"disambiguationData":[TD([[makeQuery(id+"F12.imprint","IMPRINT",EDGE,{"derivedFrom":subQ7}),1.0]])]}),makeQuery(id+"F12.imprint","IMPRINT",FACE,{"disambiguationData":[TD([[makeQuery(id+"F12.imprint","IMPRINT",EDGE,{"derivedFrom":subQ14}),1.0]])]}),makeQuery(id+"F12.imprint","IMPRINT",FACE,{"disambiguationData":[TD([[makeQuery(id+"F12.imprint","IMPRINT",EDGE,{"derivedFrom":subQ16}),1.0]])]}),makeQuery(id+"F12.imprint","IMPRINT",FACE,{"disambiguationData":[TD([[makeQuery(id+"F12.imprint","IMPRINT",EDGE,{"derivedFrom":subQ18}),-1.0]])]})]);}
            var Q1;
            Q1=makeQuery(id+"F5.boolean.opBoolean","SPLIT",FACE,{"disambiguationData":[TD([makeQuery(id+"F5.opExtrude","SWEPT_FACE",FACE,{"disambiguationData":[OSD([sQuery(id+"F4.wireOp",EDGE,"E41")])]})])],"derivedFrom":makeQuery(id+"F3.boolean.opBoolean","COPY",FACE,{"derivedFrom":makeQuery(id+"F3.opExtrude","CAP_FACE",FACE,{"disambiguationData":[OSD([sQuery(id+"F0.wireOp",EDGE,"E25.0"),sQuery(id+"F0.wireOp",EDGE,"E25.1"),sQuery(id+"F0.wireOp",EDGE,"E25.2"),sQuery(id+"F0.wireOp",EDGE,"E25.3"),sQuery(id+"F0.wireOp",EDGE,"E25.4"),sQuery(id+"F0.wireOp",EDGE,"E25.5"),sQuery(id+"F0.wireOp",EDGE,"E25.6"),sQuery(id+"F0.wireOp",EDGE,"E25.7")])],"isStart":false})})});
            extrude(context, id + "F13", {"entities" : qUnion([Q0]), "operationType" : NewBodyOperationType.REMOVE, "endBound" : BoundingType.UP_TO_SURFACE, "endBoundEntityFace" : qUnion([Q1]), "depth" : 25 * mm});
        }
        {
            var Q0;
            Q0=makeQuery(id+"F3.boolean.opBoolean","COPY",EDGE,{"derivedFrom":makeQuery(id+"F3.opExtrude","CAP_EDGE",EDGE,{"disambiguationData":[OSD([sQuery(id+"F0.wireOp",EDGE,"E25.6")])],"isStart":false})});
            var Q1;
            Q1=makeQuery(id+"F8.boolean.opBoolean","INTERSECT",EDGE,{"derivedFrom":[makeQuery(id+"F5.opExtrude","SWEPT_FACE",FACE,{"disambiguationData":[OSD([sQuery(id+"F4.wireOp",EDGE,"E30")])]}),makeQuery(id+"F8.opExtrude","CAP_FACE",FACE,{"disambiguationData":[OSD([sQuery(id+"F7.wireOp",EDGE,"E67")])],"isStart":false})]});
            var Q2;
            Q2=makeQuery(id+"F8.boolean.opBoolean","INTERSECT",EDGE,{"disambiguationData":[OD(1.0)],"derivedFrom":[makeQuery(id+"F5.opExtrude","SWEPT_FACE",FACE,{"disambiguationData":[OSD([sQuery(id+"F4.wireOp",EDGE,"E30")])]}),makeQuery(id+"F8.opExtrude","SWEPT_FACE",FACE,{"disambiguationData":[OSD([sQuery(id+"F7.wireOp",EDGE,"E67")])]})]});
            var Q3;
            {var subQ0=makeQuery(id+"F3.boolean.opBoolean","COPY",FACE,{"derivedFrom":makeQuery(id+"F3.opExtrude","CAP_FACE",FACE,{"disambiguationData":[OSD([sQuery(id+"F0.wireOp",EDGE,"E25.0"),sQuery(id+"F0.wireOp",EDGE,"E25.1"),sQuery(id+"F0.wireOp",EDGE,"E25.2"),sQuery(id+"F0.wireOp",EDGE,"E25.3"),sQuery(id+"F0.wireOp",EDGE,"E25.4"),sQuery(id+"F0.wireOp",EDGE,"E25.5"),sQuery(id+"F0.wireOp",EDGE,"E25.6"),sQuery(id+"F0.wireOp",EDGE,"E25.7")])],"isStart":false})});var subQ1=sQuery(id+"F4.wireOp",EDGE,"E30");Q3=makeQuery(id+"F8.boolean.opBoolean","SPLIT",EDGE,{"disambiguationData":[TD([makeQuery(id+"F5.opExtrude","SWEPT_FACE",FACE,{"disambiguationData":[OSD([sQuery(id+"F4.wireOp",EDGE,"E35.filletArc")])]})])],"derivedFrom":makeQuery(id+"F5.opExtrude","TWEAK_EDGE",EDGE,{"derivedFrom":[subQ0,makeQuery(id+"F4.imprint","IMPRINT",EDGE,{"derivedFrom":subQ1})]})});}
            var Q4;
            {var subQ0=sQuery(id+"F0.wireOp",EDGE,"E25.0");var subQ1=sQuery(id+"F0.wireOp",EDGE,"E25.1");var subQ2=sQuery(id+"F0.wireOp",EDGE,"E25.2");var subQ3=sQuery(id+"F0.wireOp",EDGE,"E25.3");var subQ4=sQuery(id+"F0.wireOp",EDGE,"E25.4");var subQ5=sQuery(id+"F0.wireOp",EDGE,"E25.5");var subQ6=sQuery(id+"F0.wireOp",EDGE,"E25.6");var subQ7=sQuery(id+"F0.wireOp",EDGE,"E25.7");Q4=makeQuery(id+"F8.boolean.opBoolean","INTERSECT",EDGE,{"derivedFrom":[makeQuery(id+"F5.boolean.opBoolean","SPLIT",FACE,{"disambiguationData":[TD([makeQuery(id+"F2.opExtrude","SWEPT_FACE",FACE,{"disambiguationData":[OSD([subQ0])]})])],"derivedFrom":makeQuery(id+"F3.boolean.opBoolean","COPY",FACE,{"derivedFrom":makeQuery(id+"F3.opExtrude","CAP_FACE",FACE,{"disambiguationData":[OSD([subQ0,subQ1,subQ2,subQ3,subQ4,subQ5,subQ6,subQ7])],"isStart":false})})}),makeQuery(id+"F8.opExtrude","SWEPT_FACE",FACE,{"disambiguationData":[OSD([sQuery(id+"F7.wireOp",EDGE,"E67")])]})]});}
            var Q5;
            Q5=makeQuery(id+"F8.boolean.opBoolean","INTERSECT",EDGE,{"disambiguationData":[OD(0.0)],"derivedFrom":[makeQuery(id+"F5.opExtrude","SWEPT_FACE",FACE,{"disambiguationData":[OSD([sQuery(id+"F4.wireOp",EDGE,"E30")])]}),makeQuery(id+"F8.opExtrude","SWEPT_FACE",FACE,{"disambiguationData":[OSD([sQuery(id+"F7.wireOp",EDGE,"E67")])]})]});
            fillet(context, id + "F14", {"entities" : qUnion([Q0, Q1, Q2, Q3, Q4, Q5]), "radius" : 3 * mm, "tangentPropagation" : true, "allowEdgeOverflow" : false});
        }
        {
            var Q0;
            Q0=makeQuery(id+"F1.opExtrude","CAP_EDGE",EDGE,{"disambiguationData":[OSD([sQuery(id+"F0.wireOp",EDGE,"E1.bottom")])],"isStart":false});
            fillet(context, id + "F15", {"entities" : qUnion([Q0]), "radius" : 2 * mm, "tangentPropagation" : true, "allowEdgeOverflow" : false});
        }
        {
            var Q0;
            {var subQ0=sQuery(id+"F0.wireOp",EDGE,"E21.filletArc");var subQ1=sQuery(id+"F0.wireOp",EDGE,"E7");var subQ2=sQuery(id+"F0.wireOp",EDGE,"E6");var subQ3=sQuery(id+"F0.wireOp",EDGE,"E5");var subQ4=sQuery(id+"F0.wireOp",EDGE,"E4");var subQ5=sQuery(id+"F0.wireOp",EDGE,"E22.filletArc");var subQ6=sQuery(id+"F0.wireOp",EDGE,"E1.bottom");var subQ7=sQuery(id+"F0.wireOp",EDGE,"E1.right");var subQ8=sQuery(id+"F0.wireOp",EDGE,"E1.top");var subQ9=sQuery(id+"F0.wireOp",EDGE,"E1.left");var subQ10=sQuery(id+"F0.wireOp",EDGE,"E23.filletArc");var subQ11=sQuery(id+"F0.wireOp",EDGE,"E24.filletArc");Q0=makeQuery(id+"F2.boolean.opBoolean","SPLIT",FACE,{"disambiguationData":[TD([makeQuery(id+"F1.opExtrude","SWEPT_FACE",FACE,{"disambiguationData":[OSD([subQ6])]})])],"derivedFrom":makeQuery(id+"F1.opExtrude","CAP_FACE",FACE,{"disambiguationData":[OSD([subQ6,subQ8,subQ9,subQ7,subQ4,subQ3,subQ2,subQ1,subQ0,subQ5,subQ10,subQ11])],"isStart":true})});}
            var sketch = newSketch(context, id + "F16", { "sketchPlane" : qUnion([Q0])});
            skLineSegment(sketch, "E79.0", {"start": v(-80, 90) * mm, "end": v(80, 90) * mm});
            skArc(sketch, "E80.0", {"start": v(-80, 90) * mm, "mid": v(-87.07, 87.07) * mm, "end": v(-90, 80) * mm});
            skLineSegment(sketch, "E81.0", {"start": v(-90, -80) * mm, "end": v(-90, 80) * mm});
            skArc(sketch, "E82.0", {"start": v(90, 80) * mm, "mid": v(87.07, 87.07) * mm, "end": v(80, 90) * mm});
            skArc(sketch, "E83.0", {"start": v(-90, -80) * mm, "mid": v(-87.07, -87.07) * mm, "end": v(-80, -90) * mm});
            skLineSegment(sketch, "E84.0", {"start": v(-80, -90) * mm, "end": v(80, -90) * mm});
            skArc(sketch, "E85.0", {"start": v(80, -90) * mm, "mid": v(87.07, -87.07) * mm, "end": v(90, -80) * mm});
            skLineSegment(sketch, "E86.0", {"start": v(90, -80) * mm, "end": v(90, 80) * mm});
            skCircle(sketch, "E87.0", {"center": v(60, 60) * mm, "radius": 4 * mm});
            skCircle(sketch, "E88.0", {"center": v(60, -60) * mm, "radius": 4 * mm});
            skCircle(sketch, "E89.0", {"center": v(-60, -60) * mm, "radius": 4 * mm});
            skCircle(sketch, "E90.0", {"center": v(-60, 60) * mm, "radius": 4 * mm});
            skArc(sketch, "E91.0", {"start": v(-54.26, 47.88) * mm, "mid": v(-58.44, 44.2) * mm, "end": v(-60, 38.83) * mm});
            skArc(sketch, "E92.0", {"start": v(54.26, 47.88) * mm, "mid": v(0, 60) * mm, "end": v(-54.26, 47.88) * mm});
            skLineSegment(sketch, "E93.0", {"start": v(-60, 38.83) * mm, "end": v(-60, -38.83) * mm});
            skArc(sketch, "E94.0", {"start": v(-60, -38.83) * mm, "mid": v(-58.44, -44.2) * mm, "end": v(-54.26, -47.88) * mm});
            skArc(sketch, "E95.0", {"start": v(-54.26, -47.88) * mm, "mid": v(0, -60) * mm, "end": v(54.26, -47.88) * mm});
            skArc(sketch, "E96.0", {"start": v(54.26, -47.88) * mm, "mid": v(58.44, -44.2) * mm, "end": v(60, -38.83) * mm});
            skLineSegment(sketch, "E97.0", {"start": v(60, 38.83) * mm, "end": v(60, -38.83) * mm});
            skLineSegment(sketch, "E98", {"start": v(0, 90) * mm, "end": v(0, 120) * mm, "construction": true});
            skLineSegment(sketch, "E99", {"start": v(-15, 120) * mm, "end": v(-15, 108) * mm});
            skLineSegment(sketch, "E100", {"start": v(-15, 108) * mm, "end": v(-33, 90) * mm});
            skLineSegment(sketch, "E101", {"start": v(15, 108) * mm, "end": v(15, 120) * mm});
            skLineSegment(sketch, "E102", {"start": v(15, 108) * mm, "end": v(33, 90) * mm});
            skCircle(sketch, "E103", {"center": v(0, 120) * mm, "radius": 6 * mm});
            skArc(sketch, "E104", {"start": v(15, 120) * mm, "mid": v(0, 135) * mm, "end": v(-15, 120) * mm});
            skLineSegment(sketch, "E105", {"start": v(90, 0) * mm, "end": v(-90, 0) * mm, "construction": true});
            skLineSegment(sketch, "E106.MirrorCS", {"start": v(15, -108) * mm, "end": v(33, -90) * mm});
            skLineSegment(sketch, "E107.MirrorCS", {"start": v(-15, -108) * mm, "end": v(-33, -90) * mm});
            skLineSegment(sketch, "E108.MirrorCS", {"start": v(-15, -120) * mm, "end": v(-15, -108) * mm});
            skArc(sketch, "E109.MirrorCS", {"start": v(15, -120) * mm, "mid": v(0, -135) * mm, "end": v(-15, -120) * mm});
            skCircle(sketch, "E110.MirrorC", {"center": v(0, -120) * mm, "radius": 6 * mm});
            skLineSegment(sketch, "E111.MirrorCS", {"start": v(15, -108) * mm, "end": v(15, -120) * mm});
            skSolve(sketch);
        }
        {
            var Q0;
            Q0=makeQuery(id+"F16.imprint","IMPRINT",FACE,{"disambiguationData":[TD([[makeQuery(id+"F16.imprint","IMPRINT",EDGE,{"derivedFrom":sQuery(id+"F16.wireOp",EDGE,"E99")}),1.0]])]});
            var Q1;
            {var subQ1=sQuery(id+"F16.wireOp",EDGE,"E80.0");Q1=makeQuery(id+"F16.imprint","IMPRINT",FACE,{"disambiguationData":[TD([[makeQuery(id+"F16.imprint","IMPRINT",EDGE,{"derivedFrom":subQ1}),1.0]])]});}
            var Q2;
            {var subQ1=sQuery(id+"F16.wireOp",EDGE,"E106.MirrorCS");Q2=makeQuery(id+"F16.imprint","IMPRINT",FACE,{"disambiguationData":[TD([[makeQuery(id+"F16.imprint","IMPRINT",EDGE,{"derivedFrom":subQ1}),1.0]])]});}
            var Q3;
            Q3=makeQuery(id+"F2.opExtrude","CAP_FACE",FACE,{"disambiguationData":[OSD([sQuery(id+"F0.wireOp",EDGE,"E12"),sQuery(id+"F0.wireOp",EDGE,"E13"),sQuery(id+"F0.wireOp",EDGE,"E14"),sQuery(id+"F0.wireOp",EDGE,"E15"),sQuery(id+"F0.wireOp",EDGE,"E17.filletArc"),sQuery(id+"F0.wireOp",EDGE,"E18.filletArc"),sQuery(id+"F0.wireOp",EDGE,"E19.filletArc"),sQuery(id+"F0.wireOp",EDGE,"E20.filletArc"),sQuery(id+"F0.wireOp",EDGE,"E25.0"),sQuery(id+"F0.wireOp",EDGE,"E25.1"),sQuery(id+"F0.wireOp",EDGE,"E25.2"),sQuery(id+"F0.wireOp",EDGE,"E25.3"),sQuery(id+"F0.wireOp",EDGE,"E25.4"),sQuery(id+"F0.wireOp",EDGE,"E25.5"),sQuery(id+"F0.wireOp",EDGE,"E25.6"),sQuery(id+"F0.wireOp",EDGE,"E25.7")])],"isStart":false});
            extrude(context, id + "F17", {"entities" : qUnion([Q0, Q1, Q2]), "endBound" : BoundingType.UP_TO_SURFACE, "endBoundEntityFace" : qUnion([Q3]), "depth" : 25 * mm});
        }
    });
